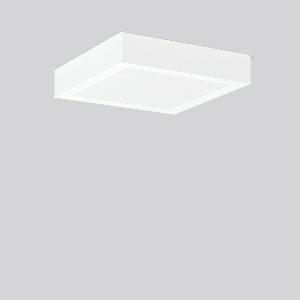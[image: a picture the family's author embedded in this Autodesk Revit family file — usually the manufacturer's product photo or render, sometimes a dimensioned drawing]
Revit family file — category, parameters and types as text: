
# Revit family: toledo_flat_square_a_672269_002_89_34ca
name_source: partatom
category: Lighting Fixtures
units: mm (PartAtom-declared; Revit-internal decimal feet)

## family parameters
Cut with Voids When Loaded = No
Host = Face
Light Source = No
Part Type = Normal
Room Calculation Point = No
Round Connector Dimension = Use Diameter
Shared = No

## types (1)
- TOLEDO FLAT square A (1 x LED Modul 830, 2050 lm, 3000)
    Apparent Load = 23 VA
    CIE Flux Codes = 48 80 96 100 100
    Color Rendering = 80
    Color Temperature = 3000
    Default Elevation = 1800 mm
    Description = Series: TOLEDO FLAT square
Ultra thin surface mounted downlight. For escape route illumination. Surface mounted housing: sheet steel, powder-coated. Square cover plate: die-cast aluminium, powder coated. Light guide and diffuser made of non-yellowing PMMA, opal matt. Driver integrated. Suitable for connection to central battery systems. With AC Control monitoring module for LUXIFAIR central battery units. 
Colour: white
Length: 300 mm
Width: 300 mm
Height: 58 mm
Weight: 3.64 kg
Operating mode: maintained power mode
Lamp: LED
Socket: without socket
Colour temperature: 3000K
Colour rendering index (CRI): 80
System power: 23 W
Rated luminous flux: 2050 lm
Luminous flux, emergency: 2050 lm
System power, emergency: 23 W
Control gear: Regulated power supply
Protection class: I
Type of protection: IP 40
    Height = 58 mm
    Lamp = 1 x LED Modul 830
    Lamp Light Flux = 2050 lm
    Lamp count = 1
    Length = 300 mm
    Lifetime = 50000 h
    Luminous efficacy = 89 lm/W
    Manufacturer = RZB
    ModVariant = No
    Model = 672269.002.89
    Mounting Place = Ceiling
    Mounting Type = Surface mounted
    Number of Poles = 1
    OnlyDefault = Yes
    Power Factor = 1
    Product Name = TOLEDO FLAT square A
    Product group = Surface mounted downlights
    ProductGroupID = 302
    Protection Class = Protection class I
    Protection Degree = IP 40
    RLX_Detail_Level = 1
    RLX_Emergency_Light_Flux = 2050 lm
    RLX_Emergency_Type = 3
    RLX_Emergency_Type_DB = Yes
    RlxData = <blob elided: 13657 chars, md5=b7b402c3>
    Socket = socket
    Standby Power = 0 W
    System Light Flux = 2050 lm
    System Power = 23 W
    Type Comments = Product without accessories
    Type Image = 901554.002.jpg
    URL = http://relux.com
    VarID = ---
    Voltage = 230 V
    Voltage Range = 220-240 V
    Weight = 0.00 kg
    Width = 300 mm

## geometry (parser evidence)
native form markers: Sweep x10
no freeform markers — native parametric forms only
